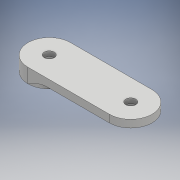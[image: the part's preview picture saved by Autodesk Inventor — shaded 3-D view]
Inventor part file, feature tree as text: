
AUTODESK INVENTOR PART (.ipt)
format: ipt  version: 2017 (Build 210142000, 142)  size: 319,488 bytes
history: native  units: mm
features: extrude x6, sketch x6, chamfer x4, hole x2, fillet x1
ambient origin geometry x8: Origin, YZ Plane, XZ Plane, XY Plane, X Axis, Y Axis, Z Axis, Center Point
bodies: Solid1 (feature_tree)
feature tree (19):
  extrude  "Extrusion1"  Depth=34.0mm
  extrude  "Extrusion2"  Depth=34.0mm
  extrude  "Extrusion3"  Depth=5.5mm
  extrude  "Extrusion4"  Depth=8.0mm
  chamfer  "Chamfer1"  Distance=3.5mm
  hole  "Hole1"  [1 undecoded]
  chamfer  "Chamfer2"  Distance=11.0mm
  extrude  "Extrusion5"  Depth=5.5mm TaperAngle=0.0deg
  extrude  "Extrusion6"  Depth=5.5mm
  chamfer  "Chamfer3"  Distance=3.5mm
  hole  "Hole2"  [1 undecoded]
  chamfer  "Chamfer4"  Distance=1.85mm Angle=45.0deg
  fillet  "Fillet2"  Radius=5.5mm
  sketch  "Sketch1"  dims[d0=65.0mm d1=34.0mm]
  sketch  "Sketch2"  dims[d2=6.0mm d3=0.0mm d4=34.0mm]
  sketch  "Sketch3"  dims[d5=5.5mm d6=0.0mm d8=11.0mm]
  sketch  "Sketch4"  dims[d9=1.0mm d10=0.0mm d11=8.0mm d12=3.5mm d13=0.0mm]
  sketch  "Sketch5"  dims[d14=1.0mm d15=2.0mm d16=45.0deg]
  sketch  "Sketch6"  dims[d51=10.0mm d52=10.0mm d19=4.3mm d20=6.0mm d21=8.0mm d22=4.0mm d23=90.0deg d24=8.0mm d25=20.594885mm d26=1.85mm d27=2.0mm d28=45.0deg d29=11.0mm d30=1.0mm d31=0.0mm d32=8.0mm d33=3.5mm d34=0.0mm d35=1.0mm d36=2.0mm d37=45.0deg d53=10.0mm d54=10.0mm d40=4.3mm d41=6.0mm d42=8.0mm d43=4.0mm d44=90.0deg d45=8.0mm d46=20.594885mm d47=1.85mm d48=2.0mm d49=45.0deg d50=5.5mm]
note: 2 required parameter values undecoded (feature->parameter linkage not recoverable at this tier; creation-order binding heuristic only, values carry confidence <= 0.55)
